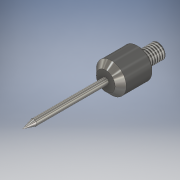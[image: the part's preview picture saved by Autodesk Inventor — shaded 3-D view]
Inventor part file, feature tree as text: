
AUTODESK INVENTOR PART (.ipt)
format: ipt  version: 2016 SP1 (Build 200210100, 210)  size: 149,504 bytes
history: native  units: in
note: dims shown in document units (in); Inventor stores cm internally (conversion verified against a paired STEP export)
features: chamfer x2, sketch x2, revolve x1, extrude x1, thread x1, projected_geometry x1
ambient origin geometry x8: Origin, YZ Plane, XZ Plane, XY Plane, X Axis, Y Axis, Z Axis, Center Point
bodies: Solid1 (feature_tree)
feature tree (8):
  revolve  "Revolution1"  [1 undecoded]
  extrude  "Extrusion1"  Depth=0.575in
  chamfer  "Chamfer1"  Angle=90.0deg  [1 undecoded]
  chamfer  "Chamfer2"  Distance=0.1181in
  thread  "Thread1"  [1 undecoded]
  sketch  "Sketch1"  dims[d0=0.1201in d1=0.26in]
  sketch  "Sketch2"  dims[d2=0.025in d3=0.575in d4=90.0deg d5=0.1181in d6=0.1575in d7=0.0in d8=0.045in d9=0.125in d10=45.0deg d11=1.0in d12=0.0in d13=75.0deg d14=15.0deg d15=0.6683in d16=0.9283in d17=0.01in d18=0.125in d19=45.0deg]
  projected_geometry  "Projected Loop1"
note: 3 required parameter values undecoded (feature->parameter linkage not recoverable at this tier; creation-order binding heuristic only, values carry confidence <= 0.55)